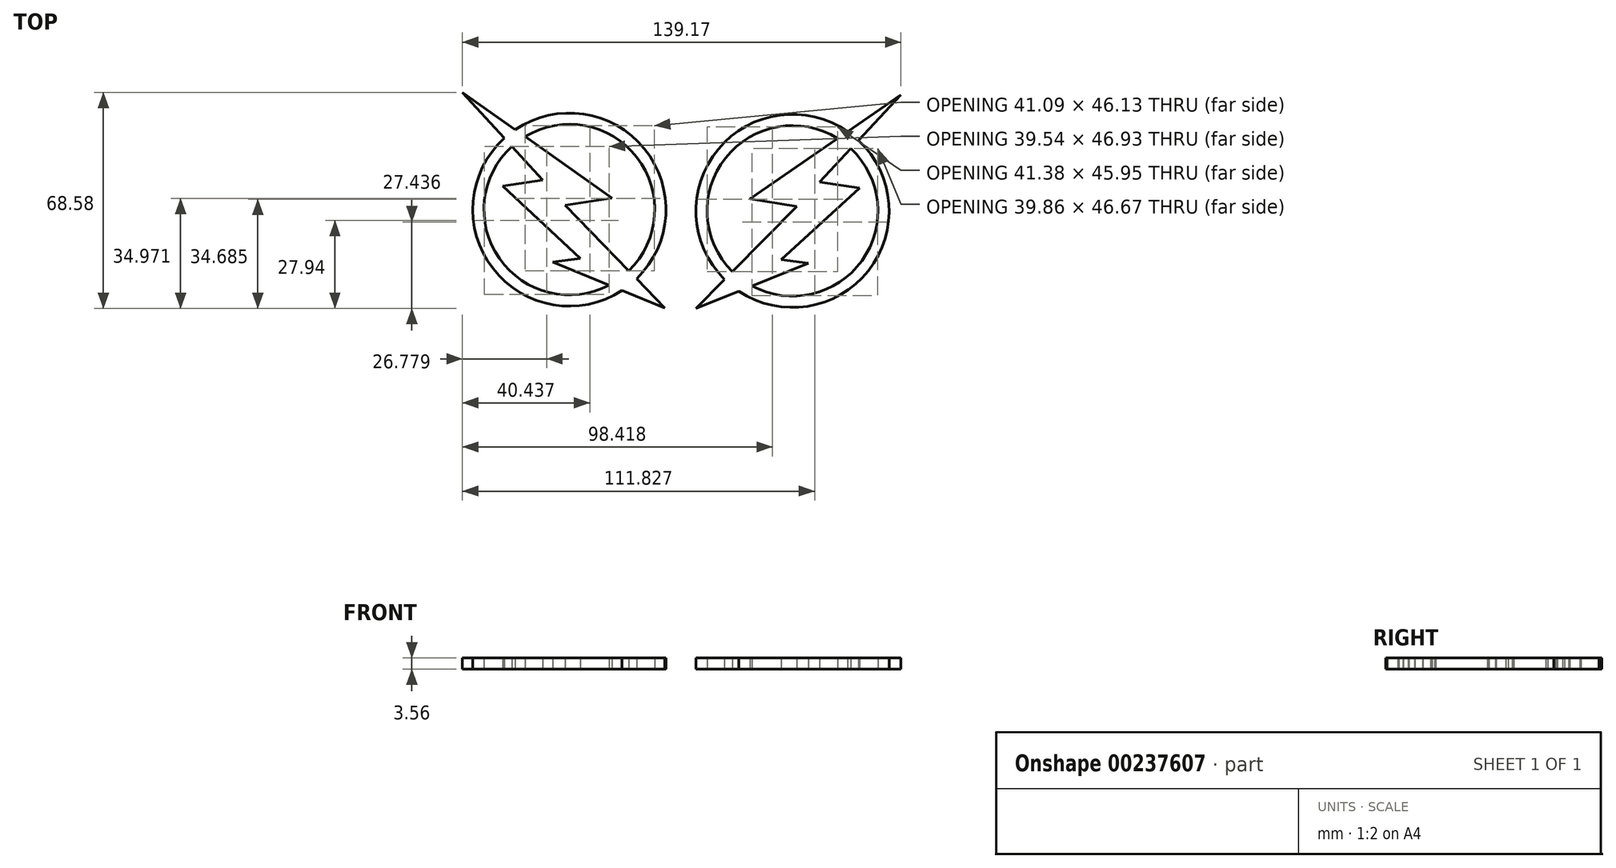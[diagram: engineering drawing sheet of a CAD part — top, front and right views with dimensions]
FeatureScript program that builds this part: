
annotation { "Feature Type Name" : "Feature", "Feature Type Description" : "" }
export const myFeature = defineFeature(function(context is Context, id is Id, definition is map)
    precondition{}
    {
        {
            var Q0;
            Q0=qCreatedBy(makeId("Top.planeOp"),FACE);
            var sketch = newSketch(context, id + "F0", { "sketchPlane" : qUnion([Q0])});
            skLineSegment(sketch, "E0", {"start": v(-69.22, 46.41) * mm, "end": v(-52.46, 34.6) * mm});
            skLineSegment(sketch, "E1", {"start": v(-21.7, 12.9) * mm, "end": v(-36.63, 10.6) * mm});
            skLineSegment(sketch, "E2", {"start": v(-36.63, 10.6) * mm, "end": v(-16.42, -10.27) * mm});
            skLineSegment(sketch, "E3", {"start": v(-4.95, -22.1) * mm, "end": v(-18.55, -16.5) * mm});
            skLineSegment(sketch, "E4", {"start": v(-40.53, -7.42) * mm, "end": v(-31.8, -6.27) * mm});
            skLineSegment(sketch, "E5", {"start": v(-31.8, -6.27) * mm, "end": v(-56.48, 16.69) * mm});
            skLineSegment(sketch, "E6", {"start": v(-56.48, 16.69) * mm, "end": v(-43.74, 18.52) * mm});
            skLineSegment(sketch, "E7", {"start": v(-43.74, 18.52) * mm, "end": v(-53.53, 29.24) * mm});
            skArc(sketch, "E8", {"start": v(-53.53, 29.24) * mm, "mid": v(-57.47, -6.35) * mm, "end": v(-22.67, -14.8) * mm});
            skArc(sketch, "E9.0", {"start": v(-55.93, 31.86) * mm, "mid": v(-59.53, -9.55) * mm, "end": v(-18.55, -16.5) * mm});
            skArc(sketch, "E10.trimOffspring", {"start": v(-16.42, -10.27) * mm, "mid": v(-13.82, 25.76) * mm, "end": v(-49.33, 32.38) * mm});
            skArc(sketch, "E11.trimOffspring", {"start": v(-13.94, -12.82) * mm, "mid": v(-11.48, 28.54) * mm, "end": v(-52.46, 34.6) * mm});
            skPoint(sketch, "E12.startSnap0", {"position": v(0.4, 53.18) * mm});
            skLineSegment(sketch, "E13.MirrorCS", {"start": v(69.95, 45.6) * mm, "end": v(53.05, 33.97) * mm});
            skLineSegment(sketch, "E14.MirrorCS", {"start": v(44.14, 18) * mm, "end": v(54.05, 28.6) * mm});
            skLineSegment(sketch, "E15.MirrorCS", {"start": v(56.86, 16.02) * mm, "end": v(44.14, 18) * mm});
            skLineSegment(sketch, "E16.MirrorCS", {"start": v(31.92, -6.64) * mm, "end": v(56.86, 16.02) * mm});
            skLineSegment(sketch, "E17.MirrorCS", {"start": v(36.93, 10.17) * mm, "end": v(16.48, -10.46) * mm});
            skLineSegment(sketch, "E18.MirrorCS", {"start": v(4.87, -22.17) * mm, "end": v(18.54, -16.71) * mm});
            skLineSegment(sketch, "E19.MirrorCS", {"start": v(40.62, -7.9) * mm, "end": v(31.92, -6.64) * mm});
            skLineSegment(sketch, "E20.MirrorCS", {"start": v(22.04, 12.64) * mm, "end": v(36.93, 10.17) * mm});
            skArc(sketch, "E21.MirrorCS", {"start": v(54.05, 28.6) * mm, "mid": v(57.57, -7.03) * mm, "end": v(22.68, -15.06) * mm});
            skArc(sketch, "E22.MirrorCS", {"start": v(16.48, -10.46) * mm, "mid": v(14.3, 25.6) * mm, "end": v(49.89, 31.8) * mm});
            skArc(sketch, "E23.MirrorCS", {"start": v(13.98, -12.98) * mm, "mid": v(12, 28.4) * mm, "end": v(53.05, 33.97) * mm});
            skArc(sketch, "E24.MirrorCS", {"start": v(56.48, 31.2) * mm, "mid": v(59.6, -10.25) * mm, "end": v(18.54, -16.71) * mm});
            skLineSegment(sketch, "E25.trimOffspring", {"start": v(-49.33, 32.38) * mm, "end": v(-21.7, 12.9) * mm});
            skLineSegment(sketch, "E26.trimOffspring", {"start": v(-55.93, 31.86) * mm, "end": v(-69.22, 46.41) * mm});
            skLineSegment(sketch, "E27.trimOffspring", {"start": v(-22.67, -14.8) * mm, "end": v(-40.53, -7.42) * mm});
            skLineSegment(sketch, "E28.trimOffspring", {"start": v(-13.94, -12.82) * mm, "end": v(-4.95, -22.1) * mm});
            skLineSegment(sketch, "E29.trimOffspring", {"start": v(22.68, -15.06) * mm, "end": v(40.62, -7.9) * mm});
            skLineSegment(sketch, "E30.trimOffspring", {"start": v(13.98, -12.98) * mm, "end": v(4.87, -22.17) * mm});
            skLineSegment(sketch, "E31.trimOffspring", {"start": v(49.89, 31.8) * mm, "end": v(22.04, 12.64) * mm});
            skLineSegment(sketch, "E32.trimOffspring", {"start": v(56.48, 31.2) * mm, "end": v(69.95, 45.6) * mm});
            skSolve(sketch);
        }
        {
            var Q0;
            Q0=makeQuery(id+"F0.imprint","IMPRINT",FACE,{"disambiguationData":[TD([[makeQuery(id+"F0.imprint","IMPRINT",EDGE,{"derivedFrom":sQuery(id+"F0.wireOp",EDGE,"E0")}),-1.0]])]});
            var Q1;
            Q1=makeQuery(id+"F0.imprint","IMPRINT",FACE,{"disambiguationData":[TD([[makeQuery(id+"F0.imprint","IMPRINT",EDGE,{"derivedFrom":sQuery(id+"F0.wireOp",EDGE,"E13.MirrorCS")}),1.0]])]});
            extrude(context, id + "F1", {"entities" : qUnion([Q0, Q1]), "depth" : 3.56 * mm});
        }
    });
